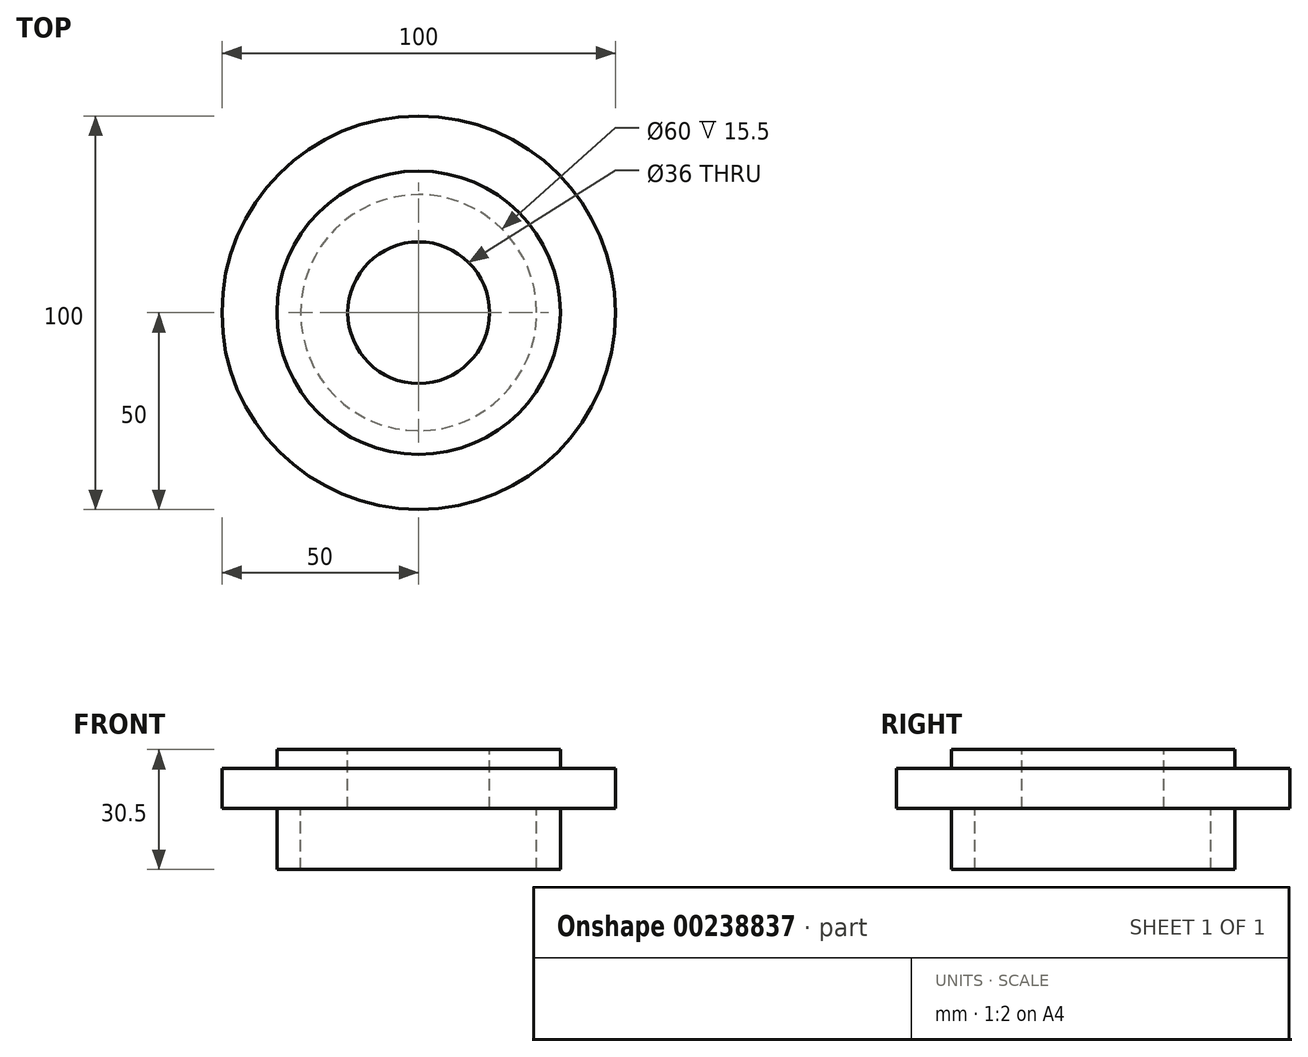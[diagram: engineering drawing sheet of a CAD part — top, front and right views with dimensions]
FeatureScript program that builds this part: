
annotation { "Feature Type Name" : "Feature", "Feature Type Description" : "" }
export const myFeature = defineFeature(function(context is Context, id is Id, definition is map)
    precondition{}
    {
        {
            var Q0;
            Q0=qCreatedBy(makeId("Front.planeOp"),FACE);
            var sketch = newSketch(context, id + "F0", { "sketchPlane" : qUnion([Q0])});
            skLineSegment(sketch, "E0", {"start": v(0, 21.98) * mm, "end": v(0, -23.76) * mm, "construction": true});
            skLineSegment(sketch, "E1", {"start": v(25.5, -0.72) * mm, "end": v(30, -0.72) * mm});
            skLineSegment(sketch, "E2", {"start": v(30, -0.72) * mm, "end": v(30, -16.22) * mm});
            skLineSegment(sketch, "E3", {"start": v(30, -16.22) * mm, "end": v(36, -16.22) * mm});
            skLineSegment(sketch, "E4", {"start": v(36, 14.28) * mm, "end": v(18, 14.28) * mm});
            skLineSegment(sketch, "E5", {"start": v(36, -16.22) * mm, "end": v(36, -0.72) * mm});
            skLineSegment(sketch, "E6", {"start": v(36, -0.72) * mm, "end": v(50, -0.72) * mm});
            skLineSegment(sketch, "E7", {"start": v(50, -0.72) * mm, "end": v(50, 9.48) * mm});
            skLineSegment(sketch, "E8", {"start": v(50, 9.48) * mm, "end": v(36, 9.48) * mm});
            skLineSegment(sketch, "E9", {"start": v(36, 9.48) * mm, "end": v(36, 14.28) * mm});
            skLineSegment(sketch, "E10", {"start": v(18, 14.28) * mm, "end": v(18, 9.48) * mm});
            skLineSegment(sketch, "E11", {"start": v(18, 9.48) * mm, "end": v(18, -0.72) * mm});
            skLineSegment(sketch, "E12", {"start": v(18, -0.72) * mm, "end": v(25.5, -0.72) * mm});
            skSolve(sketch);
        }
        {
            var Q0;
            Q0=makeQuery(id+"F0.imprint","IMPRINT",FACE,{"disambiguationData":[TD([[makeQuery(id+"F0.imprint","IMPRINT",EDGE,{"derivedFrom":sQuery(id+"F0.wireOp",EDGE,"E1")}),1.0]])]});
            var Q1;
            Q1=sQuery(id+"F0.wireOp",EDGE,"E0");
            revolve(context, id + "F1", {"entities" : qUnion([Q0]), "axis" : qUnion([Q1]), "revolveType" : RevolveType.FULL});
        }
    });
